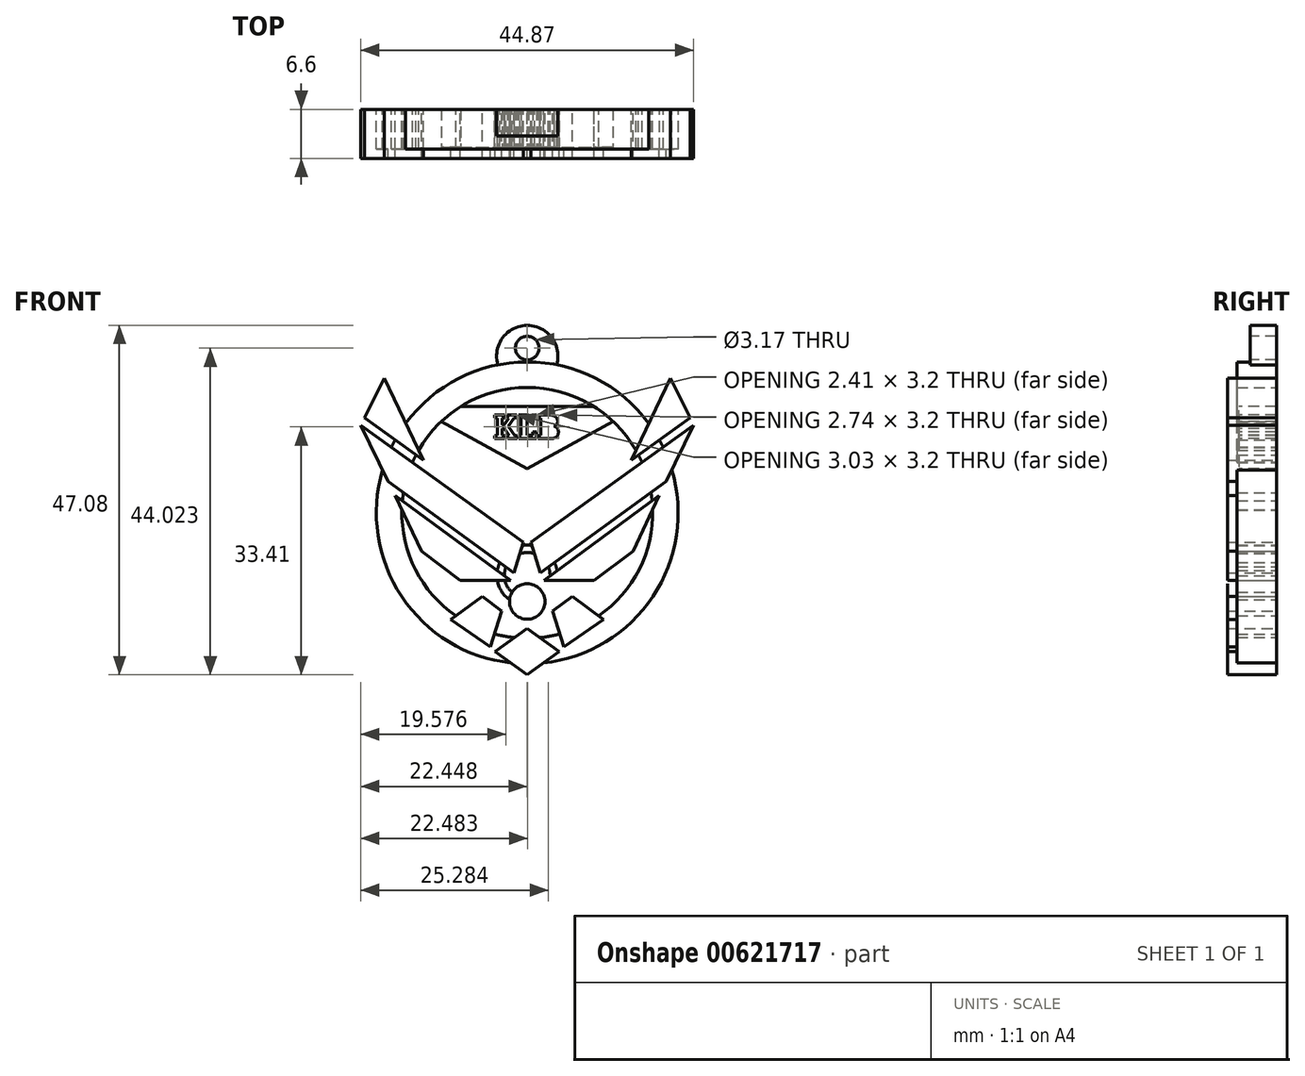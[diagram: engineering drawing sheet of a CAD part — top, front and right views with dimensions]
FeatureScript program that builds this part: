
annotation { "Feature Type Name" : "Feature", "Feature Type Description" : "" }
export const myFeature = defineFeature(function(context is Context, id is Id, definition is map)
    precondition{}
    {
        {
            var Q0;
            Q0=qCreatedBy(makeId("Front.planeOp"),FACE);
            var sketch = newSketch(context, id + "F0", { "sketchPlane" : qUnion([Q0])});
            skLineSegment(sketch, "E0", {"start": v(-11.75, -13.54) * mm, "end": v(-7.45, -10.45) * mm});
            skLineSegment(sketch, "E1", {"start": v(-11.75, -13.54) * mm, "end": v(-7.45, -16.7) * mm});
            skArc(sketch, "E2", {"start": v(-7.43, -4.4) * mm, "mid": v(-9.82, -6.8) * mm, "end": v(-7.43, -9.2) * mm});
            skLineSegment(sketch, "E3", {"start": v(-13.5, -6.12) * mm, "end": v(-10.86, -8.08) * mm});
            skLineSegment(sketch, "E4", {"start": v(-10.86, -8.08) * mm, "end": v(-12.4, -12.94) * mm});
            skLineSegment(sketch, "E5", {"start": v(-12.4, -12.94) * mm, "end": v(-17.74, -9.24) * mm});
            skLineSegment(sketch, "E6", {"start": v(-17.74, -9.24) * mm, "end": v(-13.5, -6.12) * mm});
            skLineSegment(sketch, "E7", {"start": v(-25.25, 7.48) * mm, "end": v(-21.7, 0) * mm});
            skLineSegment(sketch, "E8", {"start": v(-21.7, 0) * mm, "end": v(-16.47, -3.95) * mm});
            skLineSegment(sketch, "E9", {"start": v(-16.47, -3.95) * mm, "end": v(-9.7, -3.95) * mm});
            skLineSegment(sketch, "E10", {"start": v(-9.7, -3.95) * mm, "end": v(-25.25, 7.48) * mm});
            skLineSegment(sketch, "E11", {"start": v(-29.88, 16.94) * mm, "end": v(-7.95, 1.18) * mm});
            skLineSegment(sketch, "E12", {"start": v(-7.95, 1.18) * mm, "end": v(-9.22, -2.92) * mm});
            skLineSegment(sketch, "E13", {"start": v(-9.22, -2.92) * mm, "end": v(-26.2, 9.35) * mm});
            skLineSegment(sketch, "E14", {"start": v(-26.2, 9.35) * mm, "end": v(-29.88, 16.94) * mm});
            skLineSegment(sketch, "E15", {"start": v(-29.39, 17.92) * mm, "end": v(-21.44, 12.2) * mm});
            skLineSegment(sketch, "E16", {"start": v(-21.44, 12.2) * mm, "end": v(-26.72, 23.3) * mm});
            skLineSegment(sketch, "E17", {"start": v(-26.72, 23.3) * mm, "end": v(-29.39, 17.92) * mm});
            skArc(sketch, "E18.MirrorCS", {"start": v(-7.45, -4.4) * mm, "mid": v(-5.05, -6.8) * mm, "end": v(-7.45, -9.2) * mm});
            skLineSegment(sketch, "E19.MirrorCS", {"start": v(-3.14, -13.54) * mm, "end": v(-7.45, -10.45) * mm});
            skLineSegment(sketch, "E20.MirrorCS", {"start": v(-3.14, -13.54) * mm, "end": v(-7.45, -16.7) * mm});
            skLineSegment(sketch, "E21.MirrorCS", {"start": v(-5.67, -2.92) * mm, "end": v(11.3, 9.35) * mm});
            skLineSegment(sketch, "E22.MirrorCS", {"start": v(14.5, 17.92) * mm, "end": v(6.55, 12.2) * mm});
            skLineSegment(sketch, "E23.MirrorCS", {"start": v(11.83, 23.3) * mm, "end": v(14.5, 17.92) * mm});
            skLineSegment(sketch, "E24.MirrorCS", {"start": v(10.36, 7.48) * mm, "end": v(6.81, 0) * mm});
            skLineSegment(sketch, "E25.MirrorCS", {"start": v(2.85, -9.24) * mm, "end": v(-1.39, -6.12) * mm});
            skLineSegment(sketch, "E26.MirrorCS", {"start": v(-2.5, -12.94) * mm, "end": v(2.85, -9.24) * mm});
            skLineSegment(sketch, "E27.MirrorCS", {"start": v(-4.03, -8.08) * mm, "end": v(-2.5, -12.94) * mm});
            skLineSegment(sketch, "E28.MirrorCS", {"start": v(-1.39, -6.12) * mm, "end": v(-4.03, -8.08) * mm});
            skLineSegment(sketch, "E29.MirrorCS", {"start": v(-5.2, -3.95) * mm, "end": v(10.36, 7.48) * mm});
            skLineSegment(sketch, "E30.MirrorCS", {"start": v(1.58, -3.95) * mm, "end": v(-5.2, -3.95) * mm});
            skLineSegment(sketch, "E31.MirrorCS", {"start": v(6.81, 0) * mm, "end": v(1.58, -3.95) * mm});
            skLineSegment(sketch, "E32.MirrorCS", {"start": v(6.55, 12.2) * mm, "end": v(11.83, 23.3) * mm});
            skLineSegment(sketch, "E33.MirrorCS", {"start": v(11.3, 9.35) * mm, "end": v(14.99, 16.94) * mm});
            skLineSegment(sketch, "E34.MirrorCS", {"start": v(14.99, 16.94) * mm, "end": v(-6.94, 1.18) * mm});
            skLineSegment(sketch, "E35.MirrorCS", {"start": v(-6.94, 1.18) * mm, "end": v(-5.67, -2.92) * mm});
            skCircle(sketch, "E36", {"center": v(-7.43, 5.14) * mm, "radius": 20.33 * mm});
            skCircle(sketch, "E37", {"center": v(-7.43, 5.14) * mm, "radius": 16.9 * mm});
            skCircle(sketch, "E38", {"center": v(-7.44, -3.28) * mm, "radius": 4.07 * mm});
            skCircle(sketch, "E39", {"center": v(-7.44, -3.28) * mm, "radius": 3.07 * mm});
            skCircle(sketch, "E40", {"center": v(-7.43, 26.27) * mm, "radius": 4.13 * mm});
            skCircle(sketch, "E41", {"center": v(-7.43, 27.33) * mm, "radius": 1.59 * mm});
            skText(sketch, "E42", { "text": "KLB", "fontName": "RobotoSlab-Bold.ttf"});
            skLineSegment(sketch, "E43", {"start": v(-7.44, 18.9) * mm, "end": v(-7.44, 13.47) * mm});
            skLineSegment(sketch, "E44", {"start": v(-19, 17.46) * mm, "end": v(-7.44, 11.07) * mm});
            skLineSegment(sketch, "E45", {"start": v(-7.44, 11.07) * mm, "end": v(4.13, 17.46) * mm});
            skLineSegment(sketch, "E46", {"start": v(-16.38, 19.47) * mm, "end": v(1.52, 19.47) * mm});
            const initialGuessF0  = {"E42": [-0.01194, 0.01512, 1, 0, 0.00324]};
            skSetInitialGuess(sketch, initialGuessF0);
            skSolve(sketch);
        }
        {
            var Q0;
            {var subQ0=sQuery(id+"F0.wireOp",EDGE,"E17");Q0=makeQuery(id+"F0.imprint","IMPRINT",FACE,{"disambiguationData":[TD([[makeQuery(id+"F0.imprint","IMPRINT",EDGE,{"derivedFrom":subQ0}),1.0]])]});}
            var Q1;
            {var subQ0=sQuery(id+"F0.wireOp",EDGE,"E36");var subQ1=sQuery(id+"F0.wireOp",EDGE,"E15");var subQ2=makeQuery(id+"F0.imprint","INTERSECT",VERTEX,{"derivedFrom":[subQ1,subQ0]});Q1=makeQuery(id+"F0.imprint","IMPRINT",FACE,{"disambiguationData":[TD([[makeQuery(id+"F0.imprint","IMPRINT",EDGE,{"disambiguationData":[TD([[subQ2,-1.0]])],"derivedFrom":subQ1}),1.0]])]});}
            var Q2;
            {var subQ0=sQuery(id+"F0.wireOp",EDGE,"E16");var subQ1=sQuery(id+"F0.wireOp",EDGE,"E15");var subQ2=makeQuery(id+"F0.imprint","INTERSECT",VERTEX,{"derivedFrom":[subQ1,subQ0]});Q2=makeQuery(id+"F0.imprint","IMPRINT",FACE,{"disambiguationData":[TD([[makeQuery(id+"F0.imprint","IMPRINT",EDGE,{"disambiguationData":[TD([[subQ2,1.0]])],"derivedFrom":subQ1}),1.0]])]});}
            var Q3;
            {var subQ1=sQuery(id+"F0.wireOp",EDGE,"E11");var subQ7=sQuery(id+"F0.wireOp",EDGE,"E36");var subQ9=makeQuery(id+"F0.imprint","INTERSECT",VERTEX,{"derivedFrom":[subQ1,subQ7]});Q3=makeQuery(id+"F0.imprint","IMPRINT",FACE,{"disambiguationData":[TD([[makeQuery(id+"F0.imprint","IMPRINT",EDGE,{"disambiguationData":[TD([[subQ9,-1.0]])],"derivedFrom":subQ1}),-1.0]])]});}
            var Q4;
            {var subQ0=sQuery(id+"F0.wireOp",EDGE,"E14");var subQ1=sQuery(id+"F0.wireOp",EDGE,"E11");var subQ2=makeQuery(id+"F0.imprint","INTERSECT",VERTEX,{"derivedFrom":[subQ1,subQ0]});Q4=makeQuery(id+"F0.imprint","IMPRINT",FACE,{"disambiguationData":[TD([[makeQuery(id+"F0.imprint","IMPRINT",EDGE,{"disambiguationData":[TD([[subQ2,-1.0]])],"derivedFrom":subQ1}),-1.0]])]});}
            var Q5;
            {var subQ0=sQuery(id+"F0.wireOp",EDGE,"E12");Q5=makeQuery(id+"F0.imprint","IMPRINT",FACE,{"disambiguationData":[TD([[makeQuery(id+"F0.imprint","IMPRINT",EDGE,{"derivedFrom":subQ0}),-1.0]])]});}
            var Q6;
            {var subQ4=sQuery(id+"F0.wireOp",EDGE,"E8");Q6=makeQuery(id+"F0.imprint","IMPRINT",FACE,{"disambiguationData":[TD([[makeQuery(id+"F0.imprint","IMPRINT",EDGE,{"derivedFrom":subQ4}),1.0]])]});}
            var Q7;
            {var subQ5=sQuery(id+"F0.wireOp",EDGE,"E3");Q7=makeQuery(id+"F0.imprint","IMPRINT",FACE,{"disambiguationData":[TD([[makeQuery(id+"F0.imprint","IMPRINT",EDGE,{"derivedFrom":subQ5}),-1.0]])]});}
            var Q8;
            {var subQ0=sQuery(id+"F0.wireOp",EDGE,"E19.MirrorCS");var subQ1=sQuery(id+"F0.wireOp",EDGE,"E0");var subQ2=makeQuery(id+"F0.imprint","INTERSECT",VERTEX,{"derivedFrom":[subQ1,subQ0]});Q8=makeQuery(id+"F0.imprint","IMPRINT",FACE,{"disambiguationData":[TD([[makeQuery(id+"F0.imprint","IMPRINT",EDGE,{"disambiguationData":[TD([[subQ2,1.0]])],"derivedFrom":subQ1}),-1.0]])]});}
            var Q9;
            {var subQ7=sQuery(id+"F0.wireOp",EDGE,"E1");var subQ8=sQuery(id+"F0.wireOp",EDGE,"E0");var subQ9=makeQuery(id+"F0.imprint","INTERSECT",VERTEX,{"derivedFrom":[subQ8,subQ7]});Q9=makeQuery(id+"F0.imprint","IMPRINT",FACE,{"disambiguationData":[TD([[makeQuery(id+"F0.imprint","IMPRINT",EDGE,{"disambiguationData":[TD([[subQ9,-1.0]])],"derivedFrom":subQ8}),-1.0]])]});}
            var Q10;
            {var subQ0=sQuery(id+"F0.wireOp",EDGE,"E5");var subQ1=sQuery(id+"F0.wireOp",EDGE,"E4");var subQ2=makeQuery(id+"F0.imprint","INTERSECT",VERTEX,{"derivedFrom":[subQ1,subQ0]});Q10=makeQuery(id+"F0.imprint","IMPRINT",FACE,{"disambiguationData":[TD([[makeQuery(id+"F0.imprint","IMPRINT",EDGE,{"disambiguationData":[TD([[subQ2,1.0]])],"derivedFrom":subQ1}),-1.0]])]});}
            var Q11;
            {var subQ5=sQuery(id+"F0.wireOp",EDGE,"E25.MirrorCS");Q11=makeQuery(id+"F0.imprint","IMPRINT",FACE,{"disambiguationData":[TD([[makeQuery(id+"F0.imprint","IMPRINT",EDGE,{"derivedFrom":subQ5}),1.0]])]});}
            var Q12;
            {var subQ0=sQuery(id+"F0.wireOp",EDGE,"E27.MirrorCS");var subQ1=sQuery(id+"F0.wireOp",EDGE,"E26.MirrorCS");var subQ2=makeQuery(id+"F0.imprint","INTERSECT",VERTEX,{"derivedFrom":[subQ1,subQ0]});Q12=makeQuery(id+"F0.imprint","IMPRINT",FACE,{"disambiguationData":[TD([[makeQuery(id+"F0.imprint","IMPRINT",EDGE,{"disambiguationData":[TD([[subQ2,-1.0]])],"derivedFrom":subQ1}),1.0]])]});}
            var Q13;
            {var subQ0=sQuery(id+"F0.wireOp",EDGE,"E20.MirrorCS");var subQ1=sQuery(id+"F0.wireOp",EDGE,"E1");var subQ2=makeQuery(id+"F0.imprint","INTERSECT",VERTEX,{"derivedFrom":[subQ1,subQ0]});Q13=makeQuery(id+"F0.imprint","IMPRINT",FACE,{"disambiguationData":[TD([[makeQuery(id+"F0.imprint","IMPRINT",EDGE,{"disambiguationData":[TD([[subQ2,1.0]])],"derivedFrom":subQ1}),1.0]])]});}
            var Q14;
            {var subQ1=sQuery(id+"F0.wireOp",EDGE,"E30.MirrorCS");Q14=makeQuery(id+"F0.imprint","IMPRINT",FACE,{"disambiguationData":[TD([[makeQuery(id+"F0.imprint","IMPRINT",EDGE,{"derivedFrom":subQ1}),-1.0]])]});}
            var Q15;
            {var subQ0=sQuery(id+"F0.wireOp",EDGE,"E35.MirrorCS");Q15=makeQuery(id+"F0.imprint","IMPRINT",FACE,{"disambiguationData":[TD([[makeQuery(id+"F0.imprint","IMPRINT",EDGE,{"derivedFrom":subQ0}),1.0]])]});}
            var Q16;
            {var subQ1=sQuery(id+"F0.wireOp",EDGE,"E21.MirrorCS");var subQ7=sQuery(id+"F0.wireOp",EDGE,"E33.MirrorCS");var subQ8=makeQuery(id+"F0.imprint","INTERSECT",VERTEX,{"derivedFrom":[subQ1,subQ7]});Q16=makeQuery(id+"F0.imprint","IMPRINT",FACE,{"disambiguationData":[TD([[makeQuery(id+"F0.imprint","IMPRINT",EDGE,{"disambiguationData":[TD([[subQ8,1.0]])],"derivedFrom":subQ1}),1.0]])]});}
            var Q17;
            {var subQ0=sQuery(id+"F0.wireOp",EDGE,"E34.MirrorCS");var subQ1=sQuery(id+"F0.wireOp",EDGE,"E33.MirrorCS");var subQ2=makeQuery(id+"F0.imprint","INTERSECT",VERTEX,{"derivedFrom":[subQ1,subQ0]});Q17=makeQuery(id+"F0.imprint","IMPRINT",FACE,{"disambiguationData":[TD([[makeQuery(id+"F0.imprint","IMPRINT",EDGE,{"disambiguationData":[TD([[subQ2,1.0]])],"derivedFrom":subQ1}),1.0]])]});}
            var Q18;
            {var subQ0=sQuery(id+"F0.wireOp",EDGE,"E23.MirrorCS");Q18=makeQuery(id+"F0.imprint","IMPRINT",FACE,{"disambiguationData":[TD([[makeQuery(id+"F0.imprint","IMPRINT",EDGE,{"derivedFrom":subQ0}),-1.0]])]});}
            var Q19;
            {var subQ0=sQuery(id+"F0.wireOp",EDGE,"E36");var subQ1=sQuery(id+"F0.wireOp",EDGE,"E22.MirrorCS");var subQ2=makeQuery(id+"F0.imprint","INTERSECT",VERTEX,{"derivedFrom":[subQ1,subQ0]});Q19=makeQuery(id+"F0.imprint","IMPRINT",FACE,{"disambiguationData":[TD([[makeQuery(id+"F0.imprint","IMPRINT",EDGE,{"disambiguationData":[TD([[subQ2,-1.0]])],"derivedFrom":subQ1}),-1.0]])]});}
            var Q20;
            {var subQ0=sQuery(id+"F0.wireOp",EDGE,"E32.MirrorCS");var subQ1=sQuery(id+"F0.wireOp",EDGE,"E22.MirrorCS");var subQ2=makeQuery(id+"F0.imprint","INTERSECT",VERTEX,{"derivedFrom":[subQ1,subQ0]});Q20=makeQuery(id+"F0.imprint","IMPRINT",FACE,{"disambiguationData":[TD([[makeQuery(id+"F0.imprint","IMPRINT",EDGE,{"disambiguationData":[TD([[subQ2,1.0]])],"derivedFrom":subQ1}),-1.0]])]});}
            var Q21;
            Q21=makeQuery(id+"F0.imprint","IMPRINT",FACE,{"disambiguationData":[TD([[makeQuery(id+"F0.imprint","IMPRINT",EDGE,{"derivedFrom":sQuery(id+"F0.wireOp",EDGE,"E2")}),1.0]])]});
            var Q22;
            {var subQ0=sQuery(id+"F0.wireOp",EDGE,"E10");var subQ1=sQuery(id+"F0.wireOp",EDGE,"E7");var subQ2=makeQuery(id+"F0.imprint","INTERSECT",VERTEX,{"derivedFrom":[subQ1,subQ0]});Q22=makeQuery(id+"F0.imprint","IMPRINT",FACE,{"disambiguationData":[TD([[makeQuery(id+"F0.imprint","IMPRINT",EDGE,{"disambiguationData":[TD([[subQ2,-1.0]])],"derivedFrom":subQ1}),1.0]])]});}
            var Q23;
            {var subQ0=sQuery(id+"F0.wireOp",EDGE,"E29.MirrorCS");var subQ1=sQuery(id+"F0.wireOp",EDGE,"E24.MirrorCS");var subQ2=makeQuery(id+"F0.imprint","INTERSECT",VERTEX,{"derivedFrom":[subQ1,subQ0]});Q23=makeQuery(id+"F0.imprint","IMPRINT",FACE,{"disambiguationData":[TD([[makeQuery(id+"F0.imprint","IMPRINT",EDGE,{"disambiguationData":[TD([[subQ2,-1.0]])],"derivedFrom":subQ1}),-1.0]])]});}
            var Q24;
            {var subQ1=sQuery(id+"F0.wireOp",EDGE,"E11");var subQ7=sQuery(id+"F0.wireOp",EDGE,"E12");var subQ8=makeQuery(id+"F0.imprint","INTERSECT",VERTEX,{"derivedFrom":[subQ1,subQ7]});Q24=makeQuery(id+"F0.imprint","IMPRINT",FACE,{"disambiguationData":[TD([[makeQuery(id+"F0.imprint","IMPRINT",EDGE,{"disambiguationData":[TD([[subQ8,1.0]])],"derivedFrom":subQ1}),-1.0]])]});}
            var Q25;
            {var subQ0=sQuery(id+"F0.wireOp",EDGE,"E38");var subQ1=sQuery(id+"F0.wireOp",EDGE,"E12");var subQ2=makeQuery(id+"F0.imprint","INTERSECT",VERTEX,{"derivedFrom":[subQ1,subQ0]});Q25=makeQuery(id+"F0.imprint","IMPRINT",FACE,{"disambiguationData":[TD([[makeQuery(id+"F0.imprint","IMPRINT",EDGE,{"disambiguationData":[TD([[subQ2,-1.0]])],"derivedFrom":subQ1}),-1.0]])]});}
            var Q26;
            {var subQ0=sQuery(id+"F0.wireOp",EDGE,"E38");var subQ1=sQuery(id+"F0.wireOp",EDGE,"E9");var subQ2=makeQuery(id+"F0.imprint","INTERSECT",VERTEX,{"derivedFrom":[subQ1,subQ0]});Q26=makeQuery(id+"F0.imprint","IMPRINT",FACE,{"disambiguationData":[TD([[makeQuery(id+"F0.imprint","IMPRINT",EDGE,{"disambiguationData":[TD([[subQ2,-1.0]])],"derivedFrom":subQ1}),1.0]])]});}
            var Q27;
            {var subQ0=sQuery(id+"F0.wireOp",EDGE,"E10");var subQ1=sQuery(id+"F0.wireOp",EDGE,"E9");var subQ2=makeQuery(id+"F0.imprint","INTERSECT",VERTEX,{"derivedFrom":[subQ1,subQ0]});Q27=makeQuery(id+"F0.imprint","IMPRINT",FACE,{"disambiguationData":[TD([[makeQuery(id+"F0.imprint","IMPRINT",EDGE,{"disambiguationData":[TD([[subQ2,1.0]])],"derivedFrom":subQ1}),1.0]])]});}
            var Q28;
            {var subQ0=sQuery(id+"F0.wireOp",EDGE,"E39");var subQ1=sQuery(id+"F0.wireOp",EDGE,"E2");var subQ2=makeQuery(id+"F0.imprint","INTERSECT",VERTEX,{"derivedFrom":[subQ1,subQ0]});Q28=makeQuery(id+"F0.imprint","IMPRINT",FACE,{"disambiguationData":[TD([[makeQuery(id+"F0.imprint","IMPRINT",EDGE,{"disambiguationData":[TD([[subQ2,-1.0]])],"derivedFrom":subQ1}),1.0]])]});}
            var Q29;
            {var subQ0=sQuery(id+"F0.wireOp",EDGE,"E39");var subQ1=sQuery(id+"F0.wireOp",EDGE,"E29.MirrorCS");var subQ2=makeQuery(id+"F0.imprint","INTERSECT",VERTEX,{"derivedFrom":[subQ1,subQ0]});Q29=makeQuery(id+"F0.imprint","IMPRINT",FACE,{"disambiguationData":[TD([[makeQuery(id+"F0.imprint","IMPRINT",EDGE,{"disambiguationData":[TD([[subQ2,-1.0]])],"derivedFrom":subQ1}),-1.0]])]});}
            var Q30;
            {var subQ0=sQuery(id+"F0.wireOp",EDGE,"E31.MirrorCS");Q30=makeQuery(id+"F0.imprint","IMPRINT",FACE,{"disambiguationData":[TD([[makeQuery(id+"F0.imprint","IMPRINT",EDGE,{"derivedFrom":subQ0}),-1.0]])]});}
            var Q31;
            {var subQ0=sQuery(id+"F0.wireOp",EDGE,"E39");var subQ1=sQuery(id+"F0.wireOp",EDGE,"E21.MirrorCS");var subQ2=makeQuery(id+"F0.imprint","INTERSECT",VERTEX,{"derivedFrom":[subQ1,subQ0]});Q31=makeQuery(id+"F0.imprint","IMPRINT",FACE,{"disambiguationData":[TD([[makeQuery(id+"F0.imprint","IMPRINT",EDGE,{"disambiguationData":[TD([[subQ2,-1.0]])],"derivedFrom":subQ1}),1.0]])]});}
            var Q32;
            {var subQ1=sQuery(id+"F0.wireOp",EDGE,"E21.MirrorCS");var subQ7=sQuery(id+"F0.wireOp",EDGE,"E38");var subQ9=makeQuery(id+"F0.imprint","INTERSECT",VERTEX,{"derivedFrom":[subQ1,subQ7]});Q32=makeQuery(id+"F0.imprint","IMPRINT",FACE,{"disambiguationData":[TD([[makeQuery(id+"F0.imprint","IMPRINT",EDGE,{"disambiguationData":[TD([[subQ9,-1.0]])],"derivedFrom":subQ1}),1.0]])]});}
            extrude(context, id + "F1", {"entities" : qUnion([Q0, Q1, Q2, Q3, Q4, Q5, Q6, Q7, Q8, Q9, Q10, Q11, Q12, Q13, Q14, Q15, Q16, Q17, Q18, Q19, Q20, Q21, Q22, Q23, Q24, Q25, Q26, Q27, Q28, Q29, Q30, Q31, Q32]), "depth" : 1.52 * mm});
        }
        {
            var Q0;
            {var subQ0=sQuery(id+"F0.wireOp",EDGE,"E36");var subQ1=sQuery(id+"F0.wireOp",EDGE,"E16");var subQ2=makeQuery(id+"F0.imprint","INTERSECT",VERTEX,{"derivedFrom":[subQ1,subQ0]});Q0=makeQuery(id+"F0.imprint","IMPRINT",FACE,{"disambiguationData":[TD([[makeQuery(id+"F0.imprint","IMPRINT",EDGE,{"disambiguationData":[TD([[subQ2,1.0]])],"derivedFrom":subQ1}),-1.0]])]});}
            var Q1;
            {var subQ0=sQuery(id+"F0.wireOp",EDGE,"E36");var subQ1=sQuery(id+"F0.wireOp",EDGE,"E22.MirrorCS");var subQ2=makeQuery(id+"F0.imprint","INTERSECT",VERTEX,{"derivedFrom":[subQ1,subQ0]});Q1=makeQuery(id+"F0.imprint","IMPRINT",FACE,{"disambiguationData":[TD([[makeQuery(id+"F0.imprint","IMPRINT",EDGE,{"disambiguationData":[TD([[subQ2,-1.0]])],"derivedFrom":subQ1}),1.0]])]});}
            var Q2;
            {var subQ0=sQuery(id+"F0.wireOp",EDGE,"E36");var subQ1=sQuery(id+"F0.wireOp",EDGE,"E22.MirrorCS");var subQ2=makeQuery(id+"F0.imprint","INTERSECT",VERTEX,{"derivedFrom":[subQ1,subQ0]});Q2=makeQuery(id+"F0.imprint","IMPRINT",FACE,{"disambiguationData":[TD([[makeQuery(id+"F0.imprint","IMPRINT",EDGE,{"disambiguationData":[TD([[subQ2,-1.0]])],"derivedFrom":subQ1}),-1.0]])]});}
            var Q3;
            {var subQ1=sQuery(id+"F0.wireOp",EDGE,"E21.MirrorCS");var subQ7=sQuery(id+"F0.wireOp",EDGE,"E33.MirrorCS");var subQ8=makeQuery(id+"F0.imprint","INTERSECT",VERTEX,{"derivedFrom":[subQ1,subQ7]});Q3=makeQuery(id+"F0.imprint","IMPRINT",FACE,{"disambiguationData":[TD([[makeQuery(id+"F0.imprint","IMPRINT",EDGE,{"disambiguationData":[TD([[subQ8,1.0]])],"derivedFrom":subQ1}),1.0]])]});}
            var Q4;
            {var subQ1=sQuery(id+"F0.wireOp",EDGE,"E19.MirrorCS");var subQ15=sQuery(id+"F0.wireOp",EDGE,"E20.MirrorCS");var subQ16=makeQuery(id+"F0.imprint","INTERSECT",VERTEX,{"derivedFrom":[subQ1,subQ15]});Q4=makeQuery(id+"F0.imprint","IMPRINT",FACE,{"disambiguationData":[TD([[makeQuery(id+"F0.imprint","IMPRINT",EDGE,{"disambiguationData":[TD([[subQ16,-1.0]])],"derivedFrom":subQ1}),-1.0]])]});}
            var Q5;
            {var subQ10=sQuery(id+"F0.wireOp",EDGE,"E1");var subQ11=sQuery(id+"F0.wireOp",EDGE,"E0");var subQ12=makeQuery(id+"F0.imprint","INTERSECT",VERTEX,{"derivedFrom":[subQ11,subQ10]});Q5=makeQuery(id+"F0.imprint","IMPRINT",FACE,{"disambiguationData":[TD([[makeQuery(id+"F0.imprint","IMPRINT",EDGE,{"disambiguationData":[TD([[subQ12,-1.0]])],"derivedFrom":subQ11}),1.0]])]});}
            var Q6;
            {var subQ0=sQuery(id+"F0.wireOp",EDGE,"E36");var subQ1=sQuery(id+"F0.wireOp",EDGE,"E15");var subQ2=makeQuery(id+"F0.imprint","INTERSECT",VERTEX,{"derivedFrom":[subQ1,subQ0]});Q6=makeQuery(id+"F0.imprint","IMPRINT",FACE,{"disambiguationData":[TD([[makeQuery(id+"F0.imprint","IMPRINT",EDGE,{"disambiguationData":[TD([[subQ2,-1.0]])],"derivedFrom":subQ1}),1.0]])]});}
            var Q7;
            {var subQ0=sQuery(id+"F0.wireOp",EDGE,"E36");var subQ1=sQuery(id+"F0.wireOp",EDGE,"E11");var subQ2=makeQuery(id+"F0.imprint","INTERSECT",VERTEX,{"derivedFrom":[subQ1,subQ0]});Q7=makeQuery(id+"F0.imprint","IMPRINT",FACE,{"disambiguationData":[TD([[makeQuery(id+"F0.imprint","IMPRINT",EDGE,{"disambiguationData":[TD([[subQ2,-1.0]])],"derivedFrom":subQ1}),1.0]])]});}
            var Q8;
            {var subQ1=sQuery(id+"F0.wireOp",EDGE,"E11");var subQ7=sQuery(id+"F0.wireOp",EDGE,"E36");var subQ9=makeQuery(id+"F0.imprint","INTERSECT",VERTEX,{"derivedFrom":[subQ1,subQ7]});Q8=makeQuery(id+"F0.imprint","IMPRINT",FACE,{"disambiguationData":[TD([[makeQuery(id+"F0.imprint","IMPRINT",EDGE,{"disambiguationData":[TD([[subQ9,-1.0]])],"derivedFrom":subQ1}),-1.0]])]});}
            var Q9;
            {var subQ7=sQuery(id+"F0.wireOp",EDGE,"E1");var subQ8=sQuery(id+"F0.wireOp",EDGE,"E0");var subQ9=makeQuery(id+"F0.imprint","INTERSECT",VERTEX,{"derivedFrom":[subQ8,subQ7]});Q9=makeQuery(id+"F0.imprint","IMPRINT",FACE,{"disambiguationData":[TD([[makeQuery(id+"F0.imprint","IMPRINT",EDGE,{"disambiguationData":[TD([[subQ9,-1.0]])],"derivedFrom":subQ8}),-1.0]])]});}
            var Q10;
            {var subQ0=sQuery(id+"F0.wireOp",EDGE,"E38");var subQ1=sQuery(id+"F0.wireOp",EDGE,"E12");var subQ2=makeQuery(id+"F0.imprint","INTERSECT",VERTEX,{"derivedFrom":[subQ1,subQ0]});Q10=makeQuery(id+"F0.imprint","IMPRINT",FACE,{"disambiguationData":[TD([[makeQuery(id+"F0.imprint","IMPRINT",EDGE,{"disambiguationData":[TD([[subQ2,-1.0]])],"derivedFrom":subQ1}),1.0]])]});}
            var Q11;
            {var subQ0=sQuery(id+"F0.wireOp",EDGE,"E39");var subQ1=sQuery(id+"F0.wireOp",EDGE,"E10");var subQ2=makeQuery(id+"F0.imprint","INTERSECT",VERTEX,{"derivedFrom":[subQ1,subQ0]});Q11=makeQuery(id+"F0.imprint","IMPRINT",FACE,{"disambiguationData":[TD([[makeQuery(id+"F0.imprint","IMPRINT",EDGE,{"disambiguationData":[TD([[subQ2,-1.0]])],"derivedFrom":subQ1}),-1.0]])]});}
            var Q12;
            {var subQ0=sQuery(id+"F0.wireOp",EDGE,"E39");var subQ1=sQuery(id+"F0.wireOp",EDGE,"E2");var subQ2=makeQuery(id+"F0.imprint","INTERSECT",VERTEX,{"derivedFrom":[subQ1,subQ0]});Q12=makeQuery(id+"F0.imprint","IMPRINT",FACE,{"disambiguationData":[TD([[makeQuery(id+"F0.imprint","IMPRINT",EDGE,{"disambiguationData":[TD([[subQ2,-1.0]])],"derivedFrom":subQ1}),-1.0]])]});}
            var Q13;
            {var subQ0=sQuery(id+"F0.wireOp",EDGE,"E39");var subQ1=sQuery(id+"F0.wireOp",EDGE,"E18.MirrorCS");var subQ2=makeQuery(id+"F0.imprint","INTERSECT",VERTEX,{"derivedFrom":[subQ1,subQ0]});Q13=makeQuery(id+"F0.imprint","IMPRINT",FACE,{"disambiguationData":[TD([[makeQuery(id+"F0.imprint","IMPRINT",EDGE,{"disambiguationData":[TD([[subQ2,-1.0]])],"derivedFrom":subQ1}),1.0]])]});}
            var Q14;
            {var subQ0=sQuery(id+"F0.wireOp",EDGE,"E39");var subQ1=sQuery(id+"F0.wireOp",EDGE,"E21.MirrorCS");var subQ2=makeQuery(id+"F0.imprint","INTERSECT",VERTEX,{"derivedFrom":[subQ1,subQ0]});Q14=makeQuery(id+"F0.imprint","IMPRINT",FACE,{"disambiguationData":[TD([[makeQuery(id+"F0.imprint","IMPRINT",EDGE,{"disambiguationData":[TD([[subQ2,-1.0]])],"derivedFrom":subQ1}),-1.0]])]});}
            var Q15;
            {var subQ0=sQuery(id+"F0.wireOp",EDGE,"E36");var subQ1=sQuery(id+"F0.wireOp",EDGE,"E32.MirrorCS");var subQ2=makeQuery(id+"F0.imprint","INTERSECT",VERTEX,{"derivedFrom":[subQ1,subQ0]});Q15=makeQuery(id+"F0.imprint","IMPRINT",FACE,{"disambiguationData":[TD([[makeQuery(id+"F0.imprint","IMPRINT",EDGE,{"disambiguationData":[TD([[subQ2,1.0]])],"derivedFrom":subQ1}),1.0]])]});}
            var Q16;
            {var subQ0=sQuery(id+"F0.wireOp",EDGE,"E40");var subQ1=sQuery(id+"F0.wireOp",EDGE,"E36");var subQ2=makeQuery(id+"F0.imprint","INTERSECT",VERTEX,{"disambiguationData":[OD(0.0)],"derivedFrom":[subQ1,subQ0]});Q16=makeQuery(id+"F0.imprint","IMPRINT",FACE,{"disambiguationData":[TD([[makeQuery(id+"F0.imprint","IMPRINT",EDGE,{"disambiguationData":[TD([[subQ2,-1.0]])],"derivedFrom":subQ1}),1.0]])]});}
            var Q17;
            {var subQ5=sQuery(id+"F0.wireOp",EDGE,"29c7e069-055f-4118-b34c-edf3fcd1c2af.sketch_text.stroke-1");Q17=makeQuery(id+"F0.imprint","IMPRINT",FACE,{"disambiguationData":[TD([[makeQuery(id+"F0.imprint","IMPRINT",EDGE,{"derivedFrom":subQ5}),1.0]])]});}
            extrude(context, id + "F2", {"entities" : qUnion([Q0, Q1, Q2, Q3, Q4, Q5, Q6, Q7, Q8, Q9, Q10, Q11, Q12, Q13, Q14, Q15, Q16, Q17]), "operationType" : NewBodyOperationType.ADD, "depth" : 0.25 * mm});
        }
        {
            var Q0;
            {var subQ0=sQuery(id+"F0.wireOp",EDGE,"E36");var subQ1=sQuery(id+"F0.wireOp",EDGE,"E16");var subQ2=makeQuery(id+"F0.imprint","INTERSECT",VERTEX,{"derivedFrom":[subQ1,subQ0]});Q0=makeQuery(id+"F0.imprint","IMPRINT",FACE,{"disambiguationData":[TD([[makeQuery(id+"F0.imprint","IMPRINT",EDGE,{"disambiguationData":[TD([[subQ2,1.0]])],"derivedFrom":subQ1}),-1.0]])]});}
            var Q1;
            {var subQ0=sQuery(id+"F0.wireOp",EDGE,"E36");var subQ1=sQuery(id+"F0.wireOp",EDGE,"E22.MirrorCS");var subQ2=makeQuery(id+"F0.imprint","INTERSECT",VERTEX,{"derivedFrom":[subQ1,subQ0]});Q1=makeQuery(id+"F0.imprint","IMPRINT",FACE,{"disambiguationData":[TD([[makeQuery(id+"F0.imprint","IMPRINT",EDGE,{"disambiguationData":[TD([[subQ2,-1.0]])],"derivedFrom":subQ1}),-1.0]])]});}
            var Q2;
            {var subQ0=sQuery(id+"F0.wireOp",EDGE,"E36");var subQ1=sQuery(id+"F0.wireOp",EDGE,"E22.MirrorCS");var subQ2=makeQuery(id+"F0.imprint","INTERSECT",VERTEX,{"derivedFrom":[subQ1,subQ0]});Q2=makeQuery(id+"F0.imprint","IMPRINT",FACE,{"disambiguationData":[TD([[makeQuery(id+"F0.imprint","IMPRINT",EDGE,{"disambiguationData":[TD([[subQ2,-1.0]])],"derivedFrom":subQ1}),1.0]])]});}
            var Q3;
            {var subQ1=sQuery(id+"F0.wireOp",EDGE,"E33.MirrorCS");var subQ7=sQuery(id+"F0.wireOp",EDGE,"E21.MirrorCS");var subQ8=makeQuery(id+"F0.imprint","INTERSECT",VERTEX,{"derivedFrom":[subQ7,subQ1]});Q3=makeQuery(id+"F0.imprint","IMPRINT",FACE,{"disambiguationData":[TD([[makeQuery(id+"F0.imprint","IMPRINT",EDGE,{"disambiguationData":[TD([[subQ8,1.0]])],"derivedFrom":subQ7}),1.0]])]});}
            var Q4;
            {var subQ5=sQuery(id+"F0.wireOp",EDGE,"E26.MirrorCS");Q4=makeQuery(id+"F0.imprint","IMPRINT",FACE,{"disambiguationData":[TD([[makeQuery(id+"F0.imprint","IMPRINT",EDGE,{"derivedFrom":subQ5}),-1.0]])]});}
            var Q5;
            {var subQ7=sQuery(id+"F0.wireOp",EDGE,"E1");var subQ8=sQuery(id+"F0.wireOp",EDGE,"E0");var subQ9=makeQuery(id+"F0.imprint","INTERSECT",VERTEX,{"derivedFrom":[subQ8,subQ7]});Q5=makeQuery(id+"F0.imprint","IMPRINT",FACE,{"disambiguationData":[TD([[makeQuery(id+"F0.imprint","IMPRINT",EDGE,{"disambiguationData":[TD([[subQ9,-1.0]])],"derivedFrom":subQ8}),-1.0]])]});}
            var Q6;
            {var subQ15=sQuery(id+"F0.wireOp",EDGE,"E5");Q6=makeQuery(id+"F0.imprint","IMPRINT",FACE,{"disambiguationData":[TD([[makeQuery(id+"F0.imprint","IMPRINT",EDGE,{"derivedFrom":subQ15}),1.0]])]});}
            var Q7;
            {var subQ5=sQuery(id+"F0.wireOp",EDGE,"E36");var subQ7=sQuery(id+"F0.wireOp",EDGE,"E11");var subQ8=makeQuery(id+"F0.imprint","INTERSECT",VERTEX,{"derivedFrom":[subQ7,subQ5]});Q7=makeQuery(id+"F0.imprint","IMPRINT",FACE,{"disambiguationData":[TD([[makeQuery(id+"F0.imprint","IMPRINT",EDGE,{"disambiguationData":[TD([[subQ8,-1.0]])],"derivedFrom":subQ7}),-1.0]])]});}
            var Q8;
            {var subQ0=sQuery(id+"F0.wireOp",EDGE,"E36");var subQ1=sQuery(id+"F0.wireOp",EDGE,"E11");var subQ2=makeQuery(id+"F0.imprint","INTERSECT",VERTEX,{"derivedFrom":[subQ1,subQ0]});Q8=makeQuery(id+"F0.imprint","IMPRINT",FACE,{"disambiguationData":[TD([[makeQuery(id+"F0.imprint","IMPRINT",EDGE,{"disambiguationData":[TD([[subQ2,-1.0]])],"derivedFrom":subQ1}),1.0]])]});}
            var Q9;
            {var subQ0=sQuery(id+"F0.wireOp",EDGE,"E36");var subQ1=sQuery(id+"F0.wireOp",EDGE,"E15");var subQ2=makeQuery(id+"F0.imprint","INTERSECT",VERTEX,{"derivedFrom":[subQ1,subQ0]});Q9=makeQuery(id+"F0.imprint","IMPRINT",FACE,{"disambiguationData":[TD([[makeQuery(id+"F0.imprint","IMPRINT",EDGE,{"disambiguationData":[TD([[subQ2,-1.0]])],"derivedFrom":subQ1}),1.0]])]});}
            var Q10;
            {var subQ0=sQuery(id+"F0.wireOp",EDGE,"E38");var subQ1=sQuery(id+"F0.wireOp",EDGE,"E12");var subQ2=makeQuery(id+"F0.imprint","INTERSECT",VERTEX,{"derivedFrom":[subQ1,subQ0]});Q10=makeQuery(id+"F0.imprint","IMPRINT",FACE,{"disambiguationData":[TD([[makeQuery(id+"F0.imprint","IMPRINT",EDGE,{"disambiguationData":[TD([[subQ2,-1.0]])],"derivedFrom":subQ1}),1.0]])]});}
            var Q11;
            {var subQ0=sQuery(id+"F0.wireOp",EDGE,"E39");var subQ1=sQuery(id+"F0.wireOp",EDGE,"E21.MirrorCS");var subQ2=makeQuery(id+"F0.imprint","INTERSECT",VERTEX,{"derivedFrom":[subQ1,subQ0]});Q11=makeQuery(id+"F0.imprint","IMPRINT",FACE,{"disambiguationData":[TD([[makeQuery(id+"F0.imprint","IMPRINT",EDGE,{"disambiguationData":[TD([[subQ2,-1.0]])],"derivedFrom":subQ1}),1.0]])]});}
            var Q12;
            {var subQ0=sQuery(id+"F0.wireOp",EDGE,"E39");var subQ1=sQuery(id+"F0.wireOp",EDGE,"E21.MirrorCS");var subQ2=makeQuery(id+"F0.imprint","INTERSECT",VERTEX,{"derivedFrom":[subQ1,subQ0]});Q12=makeQuery(id+"F0.imprint","IMPRINT",FACE,{"disambiguationData":[TD([[makeQuery(id+"F0.imprint","IMPRINT",EDGE,{"disambiguationData":[TD([[subQ2,-1.0]])],"derivedFrom":subQ1}),-1.0]])]});}
            var Q13;
            {var subQ0=sQuery(id+"F0.wireOp",EDGE,"E39");var subQ1=sQuery(id+"F0.wireOp",EDGE,"E18.MirrorCS");var subQ2=makeQuery(id+"F0.imprint","INTERSECT",VERTEX,{"derivedFrom":[subQ1,subQ0]});Q13=makeQuery(id+"F0.imprint","IMPRINT",FACE,{"disambiguationData":[TD([[makeQuery(id+"F0.imprint","IMPRINT",EDGE,{"disambiguationData":[TD([[subQ2,-1.0]])],"derivedFrom":subQ1}),1.0]])]});}
            var Q14;
            {var subQ0=sQuery(id+"F0.wireOp",EDGE,"E39");var subQ1=sQuery(id+"F0.wireOp",EDGE,"E2");var subQ2=makeQuery(id+"F0.imprint","INTERSECT",VERTEX,{"derivedFrom":[subQ1,subQ0]});Q14=makeQuery(id+"F0.imprint","IMPRINT",FACE,{"disambiguationData":[TD([[makeQuery(id+"F0.imprint","IMPRINT",EDGE,{"disambiguationData":[TD([[subQ2,-1.0]])],"derivedFrom":subQ1}),1.0]])]});}
            var Q15;
            {var subQ0=sQuery(id+"F0.wireOp",EDGE,"E39");var subQ1=sQuery(id+"F0.wireOp",EDGE,"E2");var subQ2=makeQuery(id+"F0.imprint","INTERSECT",VERTEX,{"derivedFrom":[subQ1,subQ0]});Q15=makeQuery(id+"F0.imprint","IMPRINT",FACE,{"disambiguationData":[TD([[makeQuery(id+"F0.imprint","IMPRINT",EDGE,{"disambiguationData":[TD([[subQ2,-1.0]])],"derivedFrom":subQ1}),-1.0]])]});}
            var Q16;
            {var subQ0=sQuery(id+"F0.wireOp",EDGE,"E39");var subQ1=sQuery(id+"F0.wireOp",EDGE,"E10");var subQ2=makeQuery(id+"F0.imprint","INTERSECT",VERTEX,{"derivedFrom":[subQ1,subQ0]});Q16=makeQuery(id+"F0.imprint","IMPRINT",FACE,{"disambiguationData":[TD([[makeQuery(id+"F0.imprint","IMPRINT",EDGE,{"disambiguationData":[TD([[subQ2,-1.0]])],"derivedFrom":subQ1}),-1.0]])]});}
            var Q17;
            {var subQ0=sQuery(id+"F0.wireOp",EDGE,"E39");var subQ1=sQuery(id+"F0.wireOp",EDGE,"E29.MirrorCS");var subQ2=makeQuery(id+"F0.imprint","INTERSECT",VERTEX,{"derivedFrom":[subQ1,subQ0]});Q17=makeQuery(id+"F0.imprint","IMPRINT",FACE,{"disambiguationData":[TD([[makeQuery(id+"F0.imprint","IMPRINT",EDGE,{"disambiguationData":[TD([[subQ2,-1.0]])],"derivedFrom":subQ1}),-1.0]])]});}
            var Q18;
            {var subQ0=sQuery(id+"F0.wireOp",EDGE,"E38");var subQ1=sQuery(id+"F0.wireOp",EDGE,"E9");var subQ2=makeQuery(id+"F0.imprint","INTERSECT",VERTEX,{"derivedFrom":[subQ1,subQ0]});Q18=makeQuery(id+"F0.imprint","IMPRINT",FACE,{"disambiguationData":[TD([[makeQuery(id+"F0.imprint","IMPRINT",EDGE,{"disambiguationData":[TD([[subQ2,-1.0]])],"derivedFrom":subQ1}),1.0]])]});}
            var Q19;
            {var subQ0=sQuery(id+"F0.wireOp",EDGE,"E38");var subQ1=sQuery(id+"F0.wireOp",EDGE,"E12");var subQ2=makeQuery(id+"F0.imprint","INTERSECT",VERTEX,{"derivedFrom":[subQ1,subQ0]});Q19=makeQuery(id+"F0.imprint","IMPRINT",FACE,{"disambiguationData":[TD([[makeQuery(id+"F0.imprint","IMPRINT",EDGE,{"disambiguationData":[TD([[subQ2,-1.0]])],"derivedFrom":subQ1}),-1.0]])]});}
            var Q20;
            {var subQ0=sQuery(id+"F0.wireOp",EDGE,"E36");var subQ1=sQuery(id+"F0.wireOp",EDGE,"E32.MirrorCS");var subQ2=makeQuery(id+"F0.imprint","INTERSECT",VERTEX,{"derivedFrom":[subQ1,subQ0]});Q20=makeQuery(id+"F0.imprint","IMPRINT",FACE,{"disambiguationData":[TD([[makeQuery(id+"F0.imprint","IMPRINT",EDGE,{"disambiguationData":[TD([[subQ2,1.0]])],"derivedFrom":subQ1}),1.0]])]});}
            var Q21;
            {var subQ0=sQuery(id+"F0.wireOp",EDGE,"E40");var subQ1=sQuery(id+"F0.wireOp",EDGE,"E36");var subQ2=makeQuery(id+"F0.imprint","INTERSECT",VERTEX,{"disambiguationData":[OD(0.0)],"derivedFrom":[subQ1,subQ0]});Q21=makeQuery(id+"F0.imprint","IMPRINT",FACE,{"disambiguationData":[TD([[makeQuery(id+"F0.imprint","IMPRINT",EDGE,{"disambiguationData":[TD([[subQ2,-1.0]])],"derivedFrom":subQ1}),1.0]])]});}
            var Q22;
            {var subQ5=sQuery(id+"F0.wireOp",EDGE,"29c7e069-055f-4118-b34c-edf3fcd1c2af.sketch_text.stroke-1");Q22=makeQuery(id+"F0.imprint","IMPRINT",FACE,{"disambiguationData":[TD([[makeQuery(id+"F0.imprint","IMPRINT",EDGE,{"derivedFrom":subQ5}),1.0]])]});}
            extrude(context, id + "F3", {"entities" : qUnion([Q0, Q1, Q2, Q3, Q4, Q5, Q6, Q7, Q8, Q9, Q10, Q11, Q12, Q13, Q14, Q15, Q16, Q17, Q18, Q19, Q20, Q21, Q22]), "operationType" : NewBodyOperationType.ADD, "oppositeDirection" : true, "depth" : 5.08 * mm});
        }
        {
            var Q0;
            {var subQ0=sQuery(id+"F0.wireOp",EDGE,"E23.MirrorCS");Q0=makeQuery(id+"F0.imprint","IMPRINT",FACE,{"disambiguationData":[TD([[makeQuery(id+"F0.imprint","IMPRINT",EDGE,{"derivedFrom":subQ0}),-1.0]])]});}
            var Q1;
            {var subQ0=sQuery(id+"F0.wireOp",EDGE,"E32.MirrorCS");var subQ1=sQuery(id+"F0.wireOp",EDGE,"E22.MirrorCS");var subQ2=makeQuery(id+"F0.imprint","INTERSECT",VERTEX,{"derivedFrom":[subQ1,subQ0]});Q1=makeQuery(id+"F0.imprint","IMPRINT",FACE,{"disambiguationData":[TD([[makeQuery(id+"F0.imprint","IMPRINT",EDGE,{"disambiguationData":[TD([[subQ2,1.0]])],"derivedFrom":subQ1}),-1.0]])]});}
            var Q2;
            {var subQ0=sQuery(id+"F0.wireOp",EDGE,"E34.MirrorCS");var subQ1=sQuery(id+"F0.wireOp",EDGE,"E33.MirrorCS");var subQ2=makeQuery(id+"F0.imprint","INTERSECT",VERTEX,{"derivedFrom":[subQ1,subQ0]});Q2=makeQuery(id+"F0.imprint","IMPRINT",FACE,{"disambiguationData":[TD([[makeQuery(id+"F0.imprint","IMPRINT",EDGE,{"disambiguationData":[TD([[subQ2,1.0]])],"derivedFrom":subQ1}),1.0]])]});}
            var Q3;
            {var subQ0=sQuery(id+"F0.wireOp",EDGE,"E35.MirrorCS");Q3=makeQuery(id+"F0.imprint","IMPRINT",FACE,{"disambiguationData":[TD([[makeQuery(id+"F0.imprint","IMPRINT",EDGE,{"derivedFrom":subQ0}),1.0]])]});}
            var Q4;
            {var subQ1=sQuery(id+"F0.wireOp",EDGE,"E30.MirrorCS");Q4=makeQuery(id+"F0.imprint","IMPRINT",FACE,{"disambiguationData":[TD([[makeQuery(id+"F0.imprint","IMPRINT",EDGE,{"derivedFrom":subQ1}),-1.0]])]});}
            var Q5;
            {var subQ0=sQuery(id+"F0.wireOp",EDGE,"E12");Q5=makeQuery(id+"F0.imprint","IMPRINT",FACE,{"disambiguationData":[TD([[makeQuery(id+"F0.imprint","IMPRINT",EDGE,{"derivedFrom":subQ0}),-1.0]])]});}
            var Q6;
            {var subQ4=sQuery(id+"F0.wireOp",EDGE,"E8");Q6=makeQuery(id+"F0.imprint","IMPRINT",FACE,{"disambiguationData":[TD([[makeQuery(id+"F0.imprint","IMPRINT",EDGE,{"derivedFrom":subQ4}),1.0]])]});}
            var Q7;
            {var subQ0=sQuery(id+"F0.wireOp",EDGE,"E3");Q7=makeQuery(id+"F0.imprint","IMPRINT",FACE,{"disambiguationData":[TD([[makeQuery(id+"F0.imprint","IMPRINT",EDGE,{"derivedFrom":subQ0}),-1.0]])]});}
            var Q8;
            {var subQ0=sQuery(id+"F0.wireOp",EDGE,"E28.MirrorCS");Q8=makeQuery(id+"F0.imprint","IMPRINT",FACE,{"disambiguationData":[TD([[makeQuery(id+"F0.imprint","IMPRINT",EDGE,{"derivedFrom":subQ0}),1.0]])]});}
            var Q9;
            Q9=makeQuery(id+"F0.imprint","IMPRINT",FACE,{"disambiguationData":[TD([[makeQuery(id+"F0.imprint","IMPRINT",EDGE,{"derivedFrom":sQuery(id+"F0.wireOp",EDGE,"E2")}),1.0]])]});
            var Q10;
            {var subQ0=sQuery(id+"F0.wireOp",EDGE,"E19.MirrorCS");var subQ1=sQuery(id+"F0.wireOp",EDGE,"E0");var subQ2=makeQuery(id+"F0.imprint","INTERSECT",VERTEX,{"derivedFrom":[subQ1,subQ0]});Q10=makeQuery(id+"F0.imprint","IMPRINT",FACE,{"disambiguationData":[TD([[makeQuery(id+"F0.imprint","IMPRINT",EDGE,{"disambiguationData":[TD([[subQ2,1.0]])],"derivedFrom":subQ1}),-1.0]])]});}
            var Q11;
            {var subQ0=sQuery(id+"F0.wireOp",EDGE,"E20.MirrorCS");var subQ1=sQuery(id+"F0.wireOp",EDGE,"E1");var subQ2=makeQuery(id+"F0.imprint","INTERSECT",VERTEX,{"derivedFrom":[subQ1,subQ0]});Q11=makeQuery(id+"F0.imprint","IMPRINT",FACE,{"disambiguationData":[TD([[makeQuery(id+"F0.imprint","IMPRINT",EDGE,{"disambiguationData":[TD([[subQ2,1.0]])],"derivedFrom":subQ1}),1.0]])]});}
            var Q12;
            {var subQ0=sQuery(id+"F0.wireOp",EDGE,"E26.MirrorCS");Q12=makeQuery(id+"F0.imprint","IMPRINT",FACE,{"disambiguationData":[TD([[makeQuery(id+"F0.imprint","IMPRINT",EDGE,{"derivedFrom":subQ0}),1.0]])]});}
            var Q13;
            {var subQ0=sQuery(id+"F0.wireOp",EDGE,"E5");Q13=makeQuery(id+"F0.imprint","IMPRINT",FACE,{"disambiguationData":[TD([[makeQuery(id+"F0.imprint","IMPRINT",EDGE,{"derivedFrom":subQ0}),-1.0]])]});}
            var Q14;
            {var subQ0=sQuery(id+"F0.wireOp",EDGE,"E14");var subQ1=sQuery(id+"F0.wireOp",EDGE,"E11");var subQ2=makeQuery(id+"F0.imprint","INTERSECT",VERTEX,{"derivedFrom":[subQ1,subQ0]});Q14=makeQuery(id+"F0.imprint","IMPRINT",FACE,{"disambiguationData":[TD([[makeQuery(id+"F0.imprint","IMPRINT",EDGE,{"disambiguationData":[TD([[subQ2,-1.0]])],"derivedFrom":subQ1}),-1.0]])]});}
            var Q15;
            {var subQ0=sQuery(id+"F0.wireOp",EDGE,"E17");Q15=makeQuery(id+"F0.imprint","IMPRINT",FACE,{"disambiguationData":[TD([[makeQuery(id+"F0.imprint","IMPRINT",EDGE,{"derivedFrom":subQ0}),1.0]])]});}
            var Q16;
            {var subQ0=sQuery(id+"F0.wireOp",EDGE,"E36");var subQ1=sQuery(id+"F0.wireOp",EDGE,"E22.MirrorCS");var subQ2=makeQuery(id+"F0.imprint","INTERSECT",VERTEX,{"derivedFrom":[subQ1,subQ0]});Q16=makeQuery(id+"F0.imprint","IMPRINT",FACE,{"disambiguationData":[TD([[makeQuery(id+"F0.imprint","IMPRINT",EDGE,{"disambiguationData":[TD([[subQ2,-1.0]])],"derivedFrom":subQ1}),-1.0]])]});}
            var Q17;
            {var subQ1=sQuery(id+"F0.wireOp",EDGE,"E33.MirrorCS");var subQ7=sQuery(id+"F0.wireOp",EDGE,"E21.MirrorCS");var subQ8=makeQuery(id+"F0.imprint","INTERSECT",VERTEX,{"derivedFrom":[subQ7,subQ1]});Q17=makeQuery(id+"F0.imprint","IMPRINT",FACE,{"disambiguationData":[TD([[makeQuery(id+"F0.imprint","IMPRINT",EDGE,{"disambiguationData":[TD([[subQ8,1.0]])],"derivedFrom":subQ7}),1.0]])]});}
            var Q18;
            {var subQ0=sQuery(id+"F0.wireOp",EDGE,"E29.MirrorCS");var subQ1=sQuery(id+"F0.wireOp",EDGE,"E24.MirrorCS");var subQ2=makeQuery(id+"F0.imprint","INTERSECT",VERTEX,{"derivedFrom":[subQ1,subQ0]});Q18=makeQuery(id+"F0.imprint","IMPRINT",FACE,{"disambiguationData":[TD([[makeQuery(id+"F0.imprint","IMPRINT",EDGE,{"disambiguationData":[TD([[subQ2,-1.0]])],"derivedFrom":subQ1}),-1.0]])]});}
            var Q19;
            {var subQ0=sQuery(id+"F0.wireOp",EDGE,"E10");var subQ1=sQuery(id+"F0.wireOp",EDGE,"E7");var subQ2=makeQuery(id+"F0.imprint","INTERSECT",VERTEX,{"derivedFrom":[subQ1,subQ0]});Q19=makeQuery(id+"F0.imprint","IMPRINT",FACE,{"disambiguationData":[TD([[makeQuery(id+"F0.imprint","IMPRINT",EDGE,{"disambiguationData":[TD([[subQ2,-1.0]])],"derivedFrom":subQ1}),1.0]])]});}
            var Q20;
            {var subQ0=sQuery(id+"F0.wireOp",EDGE,"E36");var subQ1=sQuery(id+"F0.wireOp",EDGE,"E15");var subQ2=makeQuery(id+"F0.imprint","INTERSECT",VERTEX,{"derivedFrom":[subQ1,subQ0]});Q20=makeQuery(id+"F0.imprint","IMPRINT",FACE,{"disambiguationData":[TD([[makeQuery(id+"F0.imprint","IMPRINT",EDGE,{"disambiguationData":[TD([[subQ2,-1.0]])],"derivedFrom":subQ1}),1.0]])]});}
            var Q21;
            {var subQ0=sQuery(id+"F0.wireOp",EDGE,"E16");var subQ1=sQuery(id+"F0.wireOp",EDGE,"E15");var subQ2=makeQuery(id+"F0.imprint","INTERSECT",VERTEX,{"derivedFrom":[subQ1,subQ0]});Q21=makeQuery(id+"F0.imprint","IMPRINT",FACE,{"disambiguationData":[TD([[makeQuery(id+"F0.imprint","IMPRINT",EDGE,{"disambiguationData":[TD([[subQ2,1.0]])],"derivedFrom":subQ1}),1.0]])]});}
            var Q22;
            {var subQ5=sQuery(id+"F0.wireOp",EDGE,"E36");var subQ7=sQuery(id+"F0.wireOp",EDGE,"E11");var subQ8=makeQuery(id+"F0.imprint","INTERSECT",VERTEX,{"derivedFrom":[subQ7,subQ5]});Q22=makeQuery(id+"F0.imprint","IMPRINT",FACE,{"disambiguationData":[TD([[makeQuery(id+"F0.imprint","IMPRINT",EDGE,{"disambiguationData":[TD([[subQ8,-1.0]])],"derivedFrom":subQ7}),-1.0]])]});}
            var Q23;
            {var subQ7=sQuery(id+"F0.wireOp",EDGE,"E1");var subQ8=sQuery(id+"F0.wireOp",EDGE,"E0");var subQ9=makeQuery(id+"F0.imprint","INTERSECT",VERTEX,{"derivedFrom":[subQ8,subQ7]});Q23=makeQuery(id+"F0.imprint","IMPRINT",FACE,{"disambiguationData":[TD([[makeQuery(id+"F0.imprint","IMPRINT",EDGE,{"disambiguationData":[TD([[subQ9,-1.0]])],"derivedFrom":subQ8}),-1.0]])]});}
            var Q24;
            {var subQ1=sQuery(id+"F0.wireOp",EDGE,"E21.MirrorCS");var subQ7=sQuery(id+"F0.wireOp",EDGE,"E38");var subQ9=makeQuery(id+"F0.imprint","INTERSECT",VERTEX,{"derivedFrom":[subQ1,subQ7]});Q24=makeQuery(id+"F0.imprint","IMPRINT",FACE,{"disambiguationData":[TD([[makeQuery(id+"F0.imprint","IMPRINT",EDGE,{"disambiguationData":[TD([[subQ9,-1.0]])],"derivedFrom":subQ1}),1.0]])]});}
            var Q25;
            {var subQ0=sQuery(id+"F0.wireOp",EDGE,"E31.MirrorCS");Q25=makeQuery(id+"F0.imprint","IMPRINT",FACE,{"disambiguationData":[TD([[makeQuery(id+"F0.imprint","IMPRINT",EDGE,{"derivedFrom":subQ0}),-1.0]])]});}
            var Q26;
            {var subQ1=sQuery(id+"F0.wireOp",EDGE,"E11");var subQ7=sQuery(id+"F0.wireOp",EDGE,"E12");var subQ8=makeQuery(id+"F0.imprint","INTERSECT",VERTEX,{"derivedFrom":[subQ1,subQ7]});Q26=makeQuery(id+"F0.imprint","IMPRINT",FACE,{"disambiguationData":[TD([[makeQuery(id+"F0.imprint","IMPRINT",EDGE,{"disambiguationData":[TD([[subQ8,1.0]])],"derivedFrom":subQ1}),-1.0]])]});}
            var Q27;
            {var subQ0=sQuery(id+"F0.wireOp",EDGE,"E38");var subQ1=sQuery(id+"F0.wireOp",EDGE,"E12");var subQ2=makeQuery(id+"F0.imprint","INTERSECT",VERTEX,{"derivedFrom":[subQ1,subQ0]});Q27=makeQuery(id+"F0.imprint","IMPRINT",FACE,{"disambiguationData":[TD([[makeQuery(id+"F0.imprint","IMPRINT",EDGE,{"disambiguationData":[TD([[subQ2,-1.0]])],"derivedFrom":subQ1}),-1.0]])]});}
            var Q28;
            {var subQ0=sQuery(id+"F0.wireOp",EDGE,"E39");var subQ1=sQuery(id+"F0.wireOp",EDGE,"E21.MirrorCS");var subQ2=makeQuery(id+"F0.imprint","INTERSECT",VERTEX,{"derivedFrom":[subQ1,subQ0]});Q28=makeQuery(id+"F0.imprint","IMPRINT",FACE,{"disambiguationData":[TD([[makeQuery(id+"F0.imprint","IMPRINT",EDGE,{"disambiguationData":[TD([[subQ2,-1.0]])],"derivedFrom":subQ1}),1.0]])]});}
            var Q29;
            {var subQ0=sQuery(id+"F0.wireOp",EDGE,"E39");var subQ1=sQuery(id+"F0.wireOp",EDGE,"E29.MirrorCS");var subQ2=makeQuery(id+"F0.imprint","INTERSECT",VERTEX,{"derivedFrom":[subQ1,subQ0]});Q29=makeQuery(id+"F0.imprint","IMPRINT",FACE,{"disambiguationData":[TD([[makeQuery(id+"F0.imprint","IMPRINT",EDGE,{"disambiguationData":[TD([[subQ2,-1.0]])],"derivedFrom":subQ1}),-1.0]])]});}
            var Q30;
            {var subQ0=sQuery(id+"F0.wireOp",EDGE,"E38");var subQ1=sQuery(id+"F0.wireOp",EDGE,"E9");var subQ2=makeQuery(id+"F0.imprint","INTERSECT",VERTEX,{"derivedFrom":[subQ1,subQ0]});Q30=makeQuery(id+"F0.imprint","IMPRINT",FACE,{"disambiguationData":[TD([[makeQuery(id+"F0.imprint","IMPRINT",EDGE,{"disambiguationData":[TD([[subQ2,-1.0]])],"derivedFrom":subQ1}),1.0]])]});}
            var Q31;
            {var subQ0=sQuery(id+"F0.wireOp",EDGE,"E10");var subQ1=sQuery(id+"F0.wireOp",EDGE,"E9");var subQ2=makeQuery(id+"F0.imprint","INTERSECT",VERTEX,{"derivedFrom":[subQ1,subQ0]});Q31=makeQuery(id+"F0.imprint","IMPRINT",FACE,{"disambiguationData":[TD([[makeQuery(id+"F0.imprint","IMPRINT",EDGE,{"disambiguationData":[TD([[subQ2,1.0]])],"derivedFrom":subQ1}),1.0]])]});}
            var Q32;
            {var subQ0=sQuery(id+"F0.wireOp",EDGE,"E39");var subQ1=sQuery(id+"F0.wireOp",EDGE,"E2");var subQ2=makeQuery(id+"F0.imprint","INTERSECT",VERTEX,{"derivedFrom":[subQ1,subQ0]});Q32=makeQuery(id+"F0.imprint","IMPRINT",FACE,{"disambiguationData":[TD([[makeQuery(id+"F0.imprint","IMPRINT",EDGE,{"disambiguationData":[TD([[subQ2,-1.0]])],"derivedFrom":subQ1}),1.0]])]});}
            var Q33;
            Q33=makeQuery(id+"F0.imprint","IMPRINT",FACE,{"disambiguationData":[TD([[makeQuery(id+"F0.imprint","IMPRINT",EDGE,{"derivedFrom":sQuery(id+"F0.wireOp",EDGE,"E42.sketch_text.stroke-0")}),1.0]])]});
            extrude(context, id + "F4", {"entities" : qUnion([Q0, Q1, Q2, Q3, Q4, Q5, Q6, Q7, Q8, Q9, Q10, Q11, Q12, Q13, Q14, Q15, Q16, Q17, Q18, Q19, Q20, Q21, Q22, Q23, Q24, Q25, Q26, Q27, Q28, Q29, Q30, Q31, Q32, Q33]), "operationType" : NewBodyOperationType.ADD, "oppositeDirection" : true, "depth" : 5.08 * mm});
        }
        {
            var Q0;
            Q0=makeQuery(id+"F0.imprint","IMPRINT",FACE,{"disambiguationData":[TD([[makeQuery(id+"F0.imprint","IMPRINT",EDGE,{"derivedFrom":sQuery(id+"F0.wireOp",EDGE,"E41")}),-1.0]])]});
            extrude(context, id + "F5", {"entities" : qUnion([Q0]), "operationType" : NewBodyOperationType.ADD, "oppositeDirection" : true, "depth" : 5.08 * mm});
        }
        {
            var Q0;
            Q0=makeQuery(id+"F5.opExtrude","CAP_FACE",FACE,{"disambiguationData":[OSD([sQuery(id+"F0.wireOp",EDGE,"E36"),sQuery(id+"F0.wireOp",EDGE,"E40"),sQuery(id+"F0.wireOp",EDGE,"E41")])],"isStart":true});
            extrude(context, id + "F6", {"entities" : qUnion([Q0]), "operationType" : NewBodyOperationType.REMOVE, "oppositeDirection" : true, "depth" : 1.52 * mm});
        }
    });
